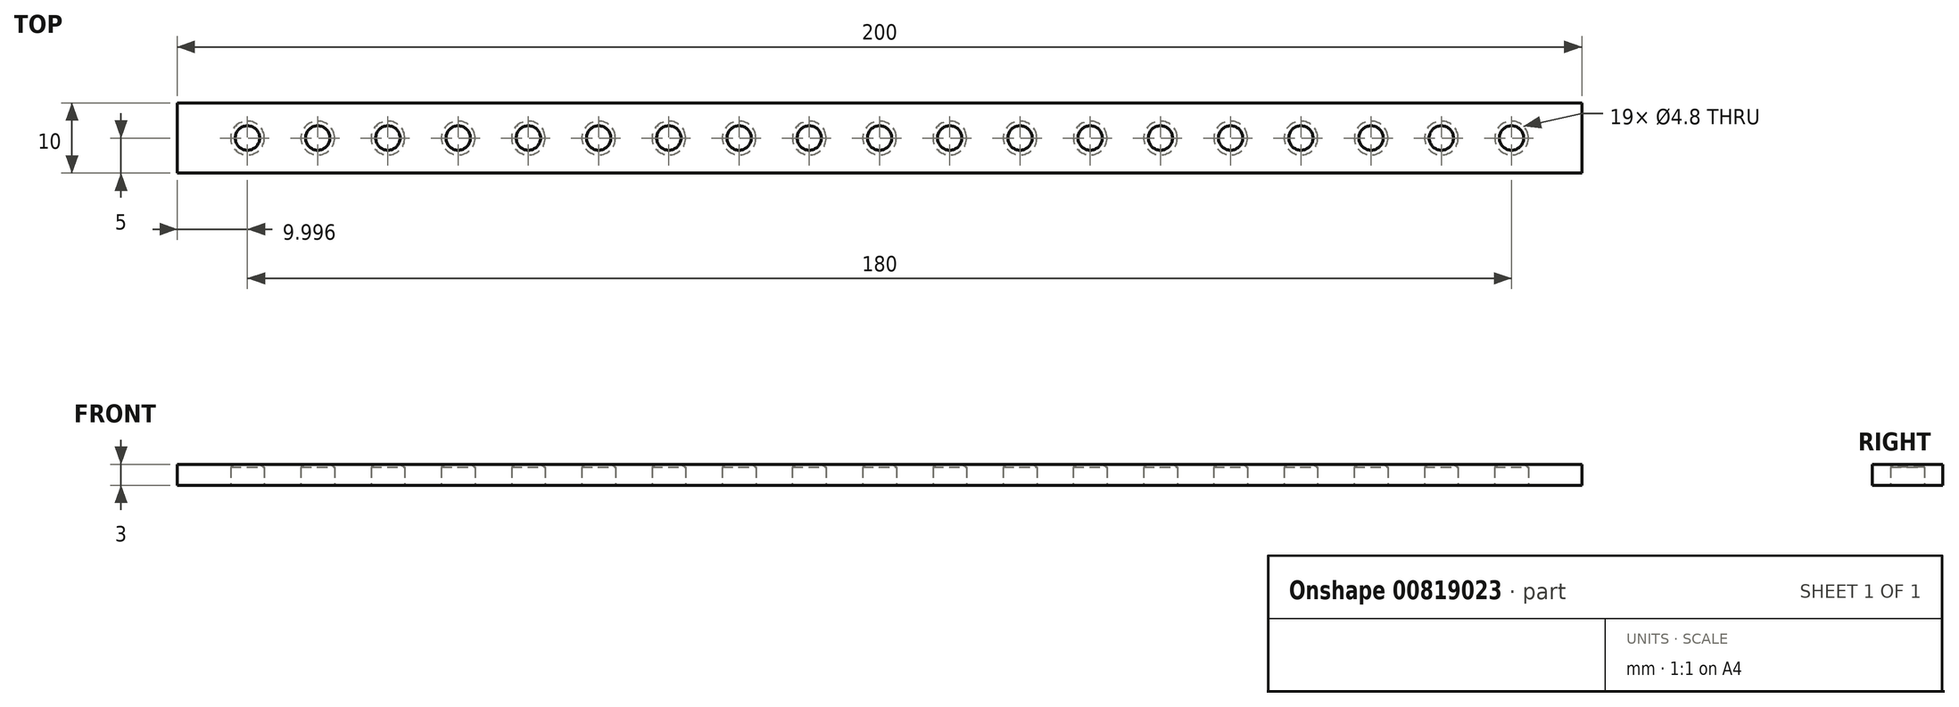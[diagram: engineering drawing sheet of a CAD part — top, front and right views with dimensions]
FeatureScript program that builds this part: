
annotation { "Feature Type Name" : "Feature", "Feature Type Description" : "" }
export const myFeature = defineFeature(function(context is Context, id is Id, definition is map)
    precondition{}
    {
        {
            var Q0;
            Q0=qCreatedBy(makeId("Top.planeOp"),FACE);
            var sketch = newSketch(context, id + "F0", { "sketchPlane" : qUnion([Q0])});
            skLineSegment(sketch, "E0.bottom", {"start": v(-100.95, 5) * mm, "end": v(99.05, 5) * mm});
            skLineSegment(sketch, "E0.top", {"start": v(-100.95, -5) * mm, "end": v(99.05, -5) * mm});
            skLineSegment(sketch, "E0.left", {"start": v(-100.95, 5) * mm, "end": v(-100.95, -5) * mm});
            skLineSegment(sketch, "E0.right", {"start": v(99.05, 5) * mm, "end": v(99.05, -5) * mm});
            skPoint(sketch, "E1", {"position": v(-90.95, 0) * mm});
            skPoint(sketch, "E2.1.0.0", {"position": v(-80.95, 0) * mm});
            skPoint(sketch, "E2.2.0.0", {"position": v(-70.95, 0) * mm});
            skPoint(sketch, "E2.3.0.0", {"position": v(-60.95, 0) * mm});
            skPoint(sketch, "E2.4.0.0", {"position": v(-50.95, 0) * mm});
            skPoint(sketch, "E2.5.0.0", {"position": v(-40.95, 0) * mm});
            skPoint(sketch, "E2.6.0.0", {"position": v(-30.95, 0) * mm});
            skPoint(sketch, "E2.7.0.0", {"position": v(-20.95, 0) * mm});
            skPoint(sketch, "E2.8.0.0", {"position": v(-10.95, 0) * mm});
            skPoint(sketch, "E2.9.0.0", {"position": v(-0.95, 0) * mm});
            skPoint(sketch, "E2.10.0.0", {"position": v(9.05, 0) * mm});
            skPoint(sketch, "E2.11.0.0", {"position": v(19.05, 0) * mm});
            skPoint(sketch, "E2.12.0.0", {"position": v(29.05, 0) * mm});
            skPoint(sketch, "E2.13.0.0", {"position": v(39.05, 0) * mm});
            skPoint(sketch, "E2.14.0.0", {"position": v(49.05, 0) * mm});
            skPoint(sketch, "E2.15.0.0", {"position": v(59.05, 0) * mm});
            skPoint(sketch, "E2.16.0.0", {"position": v(69.05, 0) * mm});
            skPoint(sketch, "E2.17.0.0", {"position": v(79.05, 0) * mm});
            skPoint(sketch, "E2.18.0.0", {"position": v(89.05, 0) * mm});
            skLineSegment(sketch, "E2.direction1", {"start": v(-90.95, 0) * mm, "end": v(-80.95, 0) * mm, "construction": true});
            skSolve(sketch);
        }
        {
            var Q0;
            Q0 = qSketchRegion(id + "F0", true);
            extrude(context, id + "F1", {"entities" : qUnion([Q0]), "depth" : 3 * mm, "offsetDistance" : 25 * mm});
        }
        {
            var Q0;
            Q0=sQuery(id+"F0.wireOp",VERTEX,"E1");
            var Q1;
            Q1=sQuery(id+"F0.wireOp",VERTEX,"E2.1.0.0");
            var Q2;
            Q2=sQuery(id+"F0.wireOp",VERTEX,"E2.2.0.0");
            var Q3;
            Q3=sQuery(id+"F0.wireOp",VERTEX,"E2.3.0.0");
            var Q4;
            Q4=sQuery(id+"F0.wireOp",VERTEX,"E2.4.0.0");
            var Q5;
            Q5=sQuery(id+"F0.wireOp",VERTEX,"E2.5.0.0");
            var Q6;
            Q6=sQuery(id+"F0.wireOp",VERTEX,"E2.6.0.0");
            var Q7;
            Q7=sQuery(id+"F0.wireOp",VERTEX,"E2.7.0.0");
            var Q8;
            Q8=sQuery(id+"F0.wireOp",VERTEX,"E2.8.0.0");
            var Q9;
            Q9=sQuery(id+"F0.wireOp",VERTEX,"E2.9.0.0");
            var Q10;
            Q10=sQuery(id+"F0.wireOp",VERTEX,"E2.10.0.0");
            var Q11;
            Q11=sQuery(id+"F0.wireOp",VERTEX,"E2.11.0.0");
            var Q12;
            Q12=sQuery(id+"F0.wireOp",VERTEX,"E2.12.0.0");
            var Q13;
            Q13=sQuery(id+"F0.wireOp",VERTEX,"E2.13.0.0");
            var Q14;
            Q14=sQuery(id+"F0.wireOp",VERTEX,"E2.14.0.0");
            var Q15;
            Q15=sQuery(id+"F0.wireOp",VERTEX,"E2.15.0.0");
            var Q16;
            Q16=sQuery(id+"F0.wireOp",VERTEX,"E2.16.0.0");
            var Q17;
            Q17=sQuery(id+"F0.wireOp",VERTEX,"E2.17.0.0");
            var Q18;
            Q18=sQuery(id+"F0.wireOp",VERTEX,"E2.18.0.0");
            var Q19;
            Q19=makeQuery(id+"F1.opExtrude","SWEPT_BODY",BODY,{"disambiguationData":[OSD([sQuery(id+"F0.wireOp",EDGE,"E0.bottom"),sQuery(id+"F0.wireOp",EDGE,"E0.top"),sQuery(id+"F0.wireOp",EDGE,"E0.left"),sQuery(id+"F0.wireOp",EDGE,"E0.right")])]});
            hole(context, id + "F2", {"style" : HoleStyle.SIMPLE, "endStyle" : HoleEndStyle.BLIND, "oppositeDirection" : true, "holeDiameter" : 4.8 * mm, "majorDiameter" : 5 * mm, "holeDepth" : 2.6 * mm, "isTappedThrough" : true, "tappedDepth" : 12 * mm, "tapClearance" : 3, "locations" : qUnion([Q0, Q1, Q2, Q3, Q4, Q5, Q6, Q7, Q8, Q9, Q10, Q11, Q12, Q13, Q14, Q15, Q16, Q17, Q18]), "scope" : qUnion([Q19])});
        }
    });
